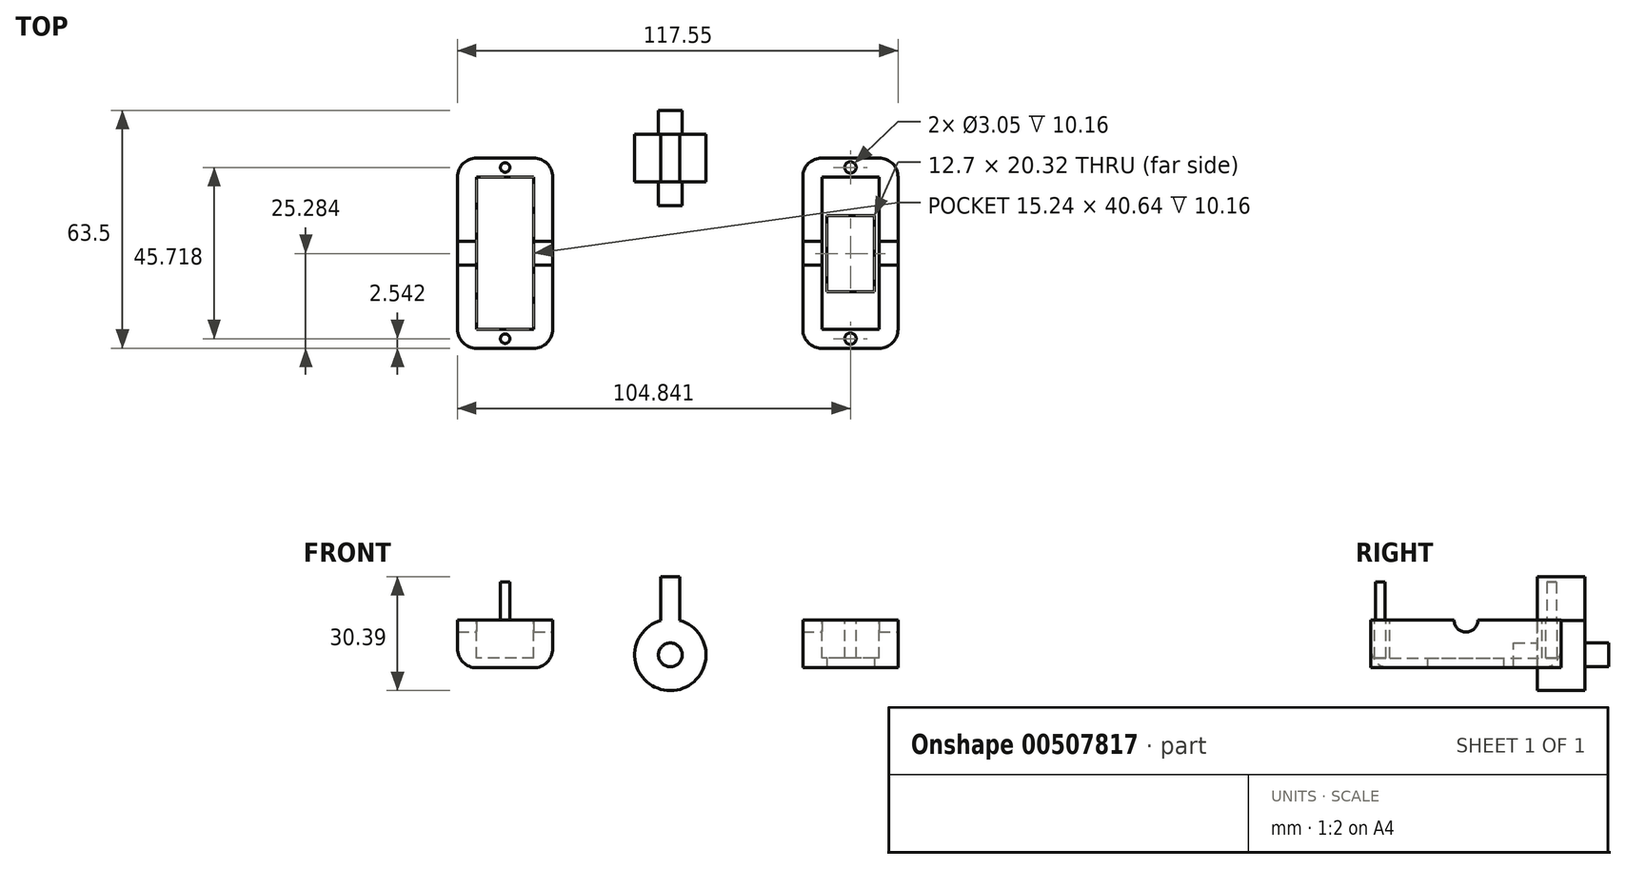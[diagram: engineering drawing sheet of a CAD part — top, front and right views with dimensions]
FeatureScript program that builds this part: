
annotation { "Feature Type Name" : "Feature", "Feature Type Description" : "" }
export const myFeature = defineFeature(function(context is Context, id is Id, definition is map)
    precondition{}
    {
        {
            var Q0;
            Q0=qCreatedBy(makeId("Front.planeOp"),FACE);
            var sketch = newSketch(context, id + "F0", { "sketchPlane" : qUnion([Q0])});
            skLineSegment(sketch, "E0", {"start": v(-56.79, 0) * mm, "end": v(-31.39, 0) * mm});
            skLineSegment(sketch, "E1", {"start": v(-31.39, 0) * mm, "end": v(-31.39, -12.7) * mm});
            skLineSegment(sketch, "E2", {"start": v(-31.39, -12.7) * mm, "end": v(-56.79, -12.7) * mm});
            skLineSegment(sketch, "E3", {"start": v(-56.79, -12.7) * mm, "end": v(-56.79, 0) * mm});
            skLineSegment(sketch, "E4", {"start": v(35.35, 0) * mm, "end": v(60.76, 0) * mm});
            skLineSegment(sketch, "E5", {"start": v(60.76, 0) * mm, "end": v(60.76, -12.7) * mm});
            skLineSegment(sketch, "E6", {"start": v(60.76, -12.7) * mm, "end": v(35.35, -12.7) * mm});
            skLineSegment(sketch, "E7", {"start": v(35.35, -12.7) * mm, "end": v(35.35, 0) * mm});
            skCircle(sketch, "E8", {"center": v(0, -9.27) * mm, "radius": 3.18 * mm});
            skCircle(sketch, "E9.0", {"center": v(0, -9.27) * mm, "radius": 9.52 * mm});
            skLineSegment(sketch, "E10", {"start": v(0, 0.26) * mm, "end": v(0, 9.15) * mm});
            skLineSegment(sketch, "E11", {"start": v(-2.54, 11.6) * mm, "end": v(-2.54, -0.09) * mm});
            skLineSegment(sketch, "E12", {"start": v(2.54, 9.15) * mm, "end": v(2.54, -0.09) * mm});
            skLineSegment(sketch, "E13", {"start": v(0, 9.15) * mm, "end": v(0, 11.6) * mm});
            skLineSegment(sketch, "E14", {"start": v(0, 11.6) * mm, "end": v(-2.54, 11.6) * mm});
            skLineSegment(sketch, "E15", {"start": v(2.54, 9.15) * mm, "end": v(2.54, 11.6) * mm});
            skLineSegment(sketch, "E16", {"start": v(2.54, 11.6) * mm, "end": v(0, 11.6) * mm});
            skSolve(sketch);
        }
        {
            var Q0;
            Q0=makeQuery(id+"F0.imprint","IMPRINT",FACE,{"disambiguationData":[TD([[makeQuery(id+"F0.imprint","IMPRINT",EDGE,{"derivedFrom":sQuery(id+"F0.wireOp",EDGE,"E4")}),-1.0]])]});
            var Q1;
            Q1=makeQuery(id+"F0.imprint","IMPRINT",FACE,{"disambiguationData":[TD([[makeQuery(id+"F0.imprint","IMPRINT",EDGE,{"derivedFrom":sQuery(id+"F0.wireOp",EDGE,"E0")}),-1.0]])]});
            extrude(context, id + "F1", {"entities" : qUnion([Q0, Q1]), "depth" : 50.8 * mm});
        }
        {
            var Q0;
            Q0=qCreatedBy(makeId("Top.planeOp"),FACE);
            var sketch = newSketch(context, id + "F2", { "sketchPlane" : qUnion([Q0])});
            skLineSegment(sketch, "E17.0", {"start": v(-36.47, -5.08) * mm, "end": v(-51.7, -5.08) * mm});
            skLineSegment(sketch, "E17.1", {"start": v(-36.47, -45.72) * mm, "end": v(-36.47, -5.08) * mm});
            skLineSegment(sketch, "E17.2", {"start": v(-51.7, -45.72) * mm, "end": v(-36.47, -45.72) * mm});
            skLineSegment(sketch, "E17.3", {"start": v(-51.7, -5.08) * mm, "end": v(-51.7, -45.72) * mm});
            skLineSegment(sketch, "E18.0", {"start": v(55.68, -5.08) * mm, "end": v(40.43, -5.08) * mm});
            skLineSegment(sketch, "E18.1", {"start": v(55.68, -45.72) * mm, "end": v(55.68, -5.08) * mm});
            skLineSegment(sketch, "E18.2", {"start": v(40.43, -45.72) * mm, "end": v(55.68, -45.72) * mm});
            skLineSegment(sketch, "E18.3", {"start": v(40.43, -5.08) * mm, "end": v(40.43, -45.72) * mm});
            skCircle(sketch, "E19", {"center": v(-44.09, -48.25) * mm, "radius": 1.27 * mm});
            skCircle(sketch, "E20", {"center": v(-44.09, -2.54) * mm, "radius": 1.27 * mm});
            skCircle(sketch, "E21", {"center": v(48.05, -2.54) * mm, "radius": 1.52 * mm});
            skCircle(sketch, "E22", {"center": v(48.05, -48.26) * mm, "radius": 1.52 * mm});
            skSolve(sketch);
        }
        {
            var Q0;
            Q0=makeQuery(id+"F2.imprint","IMPRINT",FACE,{"disambiguationData":[TD([[makeQuery(id+"F2.imprint","IMPRINT",EDGE,{"derivedFrom":sQuery(id+"F2.wireOp",EDGE,"E17.0")}),1.0]])]});
            extrude(context, id + "F3", {"entities" : qUnion([Q0]), "operationType" : NewBodyOperationType.REMOVE, "oppositeDirection" : true, "depth" : 10.16 * mm});
        }
        {
            var Q0;
            Q0=makeQuery(id+"F2.imprint","IMPRINT",FACE,{"disambiguationData":[TD([[makeQuery(id+"F2.imprint","IMPRINT",EDGE,{"derivedFrom":sQuery(id+"F2.wireOp",EDGE,"E18.0")}),1.0]])]});
            extrude(context, id + "F4", {"entities" : qUnion([Q0]), "operationType" : NewBodyOperationType.REMOVE, "oppositeDirection" : true, "depth" : 10.16 * mm});
        }
        {
            var Q0;
            Q0=makeQuery(id+"F1.opExtrude","SWEPT_FACE",FACE,{"disambiguationData":[OSD([sQuery(id+"F0.wireOp",EDGE,"E1")])]});
            var sketch = newSketch(context, id + "F5", { "sketchPlane" : qUnion([Q0])});
            skCircle(sketch, "E23", {"center": v(-25.4, 0) * mm, "radius": 3.18 * mm});
            skSolve(sketch);
        }
        {
            var Q0;
            {var subQ0=sQuery(id+"F5.wireOp",EDGE,"E23");var subQ1=makeQuery(id+"F1.opExtrude","SWEPT_EDGE",EDGE,{"disambiguationData":[OSD([sQuery(id+"F0.wireOp",EDGE,"E0"),sQuery(id+"F0.wireOp",EDGE,"E1")])]});var subQ2=makeQuery(id+"F5.imprint","INTERSECT",VERTEX,{"disambiguationData":[OD(0.0)],"derivedFrom":[subQ1,subQ0]});Q0=makeQuery(id+"F5.imprint","IMPRINT",FACE,{"disambiguationData":[TD([[makeQuery(id+"F5.imprint","IMPRINT",EDGE,{"disambiguationData":[TD([[subQ2,1.0]])],"derivedFrom":subQ0}),1.0]])]});}
            extrude(context, id + "F6", {"entities" : qUnion([Q0]), "operationType" : NewBodyOperationType.REMOVE, "oppositeDirection" : true, "depth" : 25.4 * mm});
        }
        {
            var Q0;
            Q0=makeQuery(id+"F1.opExtrude","SWEPT_FACE",FACE,{"disambiguationData":[OSD([sQuery(id+"F0.wireOp",EDGE,"E5")])]});
            var sketch = newSketch(context, id + "F7", { "sketchPlane" : qUnion([Q0])});
            skCircle(sketch, "E24", {"center": v(-25.4, 0) * mm, "radius": 3.18 * mm});
            skSolve(sketch);
        }
        {
            var Q0;
            {var subQ0=sQuery(id+"F7.wireOp",EDGE,"E24");var subQ1=makeQuery(id+"F1.opExtrude","SWEPT_EDGE",EDGE,{"disambiguationData":[OSD([sQuery(id+"F0.wireOp",EDGE,"E4"),sQuery(id+"F0.wireOp",EDGE,"E5")])]});var subQ2=makeQuery(id+"F7.imprint","INTERSECT",VERTEX,{"disambiguationData":[OD(0.0)],"derivedFrom":[subQ1,subQ0]});Q0=makeQuery(id+"F7.imprint","IMPRINT",FACE,{"disambiguationData":[TD([[makeQuery(id+"F7.imprint","IMPRINT",EDGE,{"disambiguationData":[TD([[subQ2,1.0]])],"derivedFrom":subQ0}),1.0]])]});}
            extrude(context, id + "F8", {"entities" : qUnion([Q0]), "operationType" : NewBodyOperationType.REMOVE, "oppositeDirection" : true, "depth" : 25.4 * mm});
        }
        {
            var Q0;
            Q0=makeQuery(id+"F1.opExtrude","SWEPT_FACE",FACE,{"disambiguationData":[OSD([sQuery(id+"F0.wireOp",EDGE,"E6")])]});
            var sketch = newSketch(context, id + "F9", { "sketchPlane" : qUnion([Q0])});
            skLineSegment(sketch, "E25", {"start": v(41.7, 25.52) * mm, "end": v(41.7, 15.36) * mm});
            skLineSegment(sketch, "E26", {"start": v(41.7, 25.52) * mm, "end": v(41.7, 35.68) * mm});
            skLineSegment(sketch, "E27", {"start": v(54.4, 15.36) * mm, "end": v(54.4, 25.52) * mm});
            skLineSegment(sketch, "E28", {"start": v(41.7, 35.68) * mm, "end": v(54.4, 35.68) * mm});
            skLineSegment(sketch, "E29", {"start": v(54.4, 35.68) * mm, "end": v(54.4, 25.52) * mm});
            skLineSegment(sketch, "E30", {"start": v(41.7, 15.36) * mm, "end": v(54.4, 15.36) * mm});
            skLineSegment(sketch, "E31", {"start": v(41.7, 25.52) * mm, "end": v(54.4, 25.52) * mm});
            skSolve(sketch);
        }
        {
            var Q0;
            Q0=makeQuery(id+"F1.opExtrude","CAP_EDGE",EDGE,{"disambiguationData":[OSD([sQuery(id+"F0.wireOp",EDGE,"E1")])],"isStart":false});
            var Q1;
            Q1=makeQuery(id+"F1.opExtrude","CAP_EDGE",EDGE,{"disambiguationData":[OSD([sQuery(id+"F0.wireOp",EDGE,"E3")])],"isStart":false});
            var Q2;
            Q2=makeQuery(id+"F1.opExtrude","CAP_EDGE",EDGE,{"disambiguationData":[OSD([sQuery(id+"F0.wireOp",EDGE,"E2")])],"isStart":false});
            var Q3;
            Q3=makeQuery(id+"F1.opExtrude","SWEPT_EDGE",EDGE,{"disambiguationData":[OSD([sQuery(id+"F0.wireOp",EDGE,"E2"),sQuery(id+"F0.wireOp",EDGE,"E3")])]});
            var Q4;
            Q4=makeQuery(id+"F1.opExtrude","CAP_EDGE",EDGE,{"disambiguationData":[OSD([sQuery(id+"F0.wireOp",EDGE,"E3")])],"isStart":true});
            var Q5;
            Q5=makeQuery(id+"F1.opExtrude","CAP_EDGE",EDGE,{"disambiguationData":[OSD([sQuery(id+"F0.wireOp",EDGE,"E2")])],"isStart":true});
            var Q6;
            Q6=makeQuery(id+"F1.opExtrude","CAP_EDGE",EDGE,{"disambiguationData":[OSD([sQuery(id+"F0.wireOp",EDGE,"E1")])],"isStart":true});
            var Q7;
            Q7=makeQuery(id+"F1.opExtrude","SWEPT_EDGE",EDGE,{"disambiguationData":[OSD([sQuery(id+"F0.wireOp",EDGE,"E1"),sQuery(id+"F0.wireOp",EDGE,"E2")])]});
            fillet(context, id + "F10", {"entities" : qUnion([Q0, Q1, Q2, Q3, Q4, Q5, Q6, Q7]), "radius" : 5.08 * mm, "tangentPropagation" : true, "allowEdgeOverflow" : false});
        }
        {
            var Q0;
            Q0=makeQuery(id+"F0.imprint","IMPRINT",FACE,{"disambiguationData":[TD([[makeQuery(id+"F0.imprint","IMPRINT",EDGE,{"derivedFrom":sQuery(id+"F0.wireOp",EDGE,"E8")}),-1.0]])]});
            var Q1;
            {var subQ0=sQuery(id+"F0.wireOp",EDGE,"E10");Q1=makeQuery(id+"F0.imprint","IMPRINT",FACE,{"disambiguationData":[TD([[makeQuery(id+"F0.imprint","IMPRINT",EDGE,{"derivedFrom":subQ0}),-1.0]])]});}
            var Q2;
            {var subQ0=sQuery(id+"F0.wireOp",EDGE,"E10");Q2=makeQuery(id+"F0.imprint","IMPRINT",FACE,{"disambiguationData":[TD([[makeQuery(id+"F0.imprint","IMPRINT",EDGE,{"derivedFrom":subQ0}),1.0]])]});}
            extrude(context, id + "F11", {"entities" : qUnion([Q0, Q1, Q2]), "depth" : 12.7 * mm, "offsetDistance" : 25.4 * mm, "symmetric" : true});
        }
        {
            var Q0;
            Q0=makeQuery(id+"F0.imprint","IMPRINT",FACE,{"disambiguationData":[TD([[makeQuery(id+"F0.imprint","IMPRINT",EDGE,{"derivedFrom":sQuery(id+"F0.wireOp",EDGE,"E8")}),1.0]])]});
            extrude(context, id + "F12", {"entities" : qUnion([Q0]), "operationType" : NewBodyOperationType.ADD, "depth" : 25.4 * mm, "offsetDistance" : 25.4 * mm, "symmetric" : true});
        }
        {
            var Q0;
            Q0=makeQuery(id+"F2.imprint","IMPRINT",FACE,{"disambiguationData":[TD([[makeQuery(id+"F2.imprint","IMPRINT",EDGE,{"derivedFrom":sQuery(id+"F2.wireOp",EDGE,"E20")}),1.0]])]});
            var Q1;
            Q1=makeQuery(id+"F2.imprint","IMPRINT",FACE,{"disambiguationData":[TD([[makeQuery(id+"F2.imprint","IMPRINT",EDGE,{"derivedFrom":sQuery(id+"F2.wireOp",EDGE,"E19")}),1.0]])]});
            extrude(context, id + "F13", {"entities" : qUnion([Q0, Q1]), "operationType" : NewBodyOperationType.ADD, "depth" : 10.16 * mm, "offsetDistance" : 25.4 * mm});
        }
        {
            var Q0;
            Q0=makeQuery(id+"F2.imprint","IMPRINT",FACE,{"disambiguationData":[TD([[makeQuery(id+"F2.imprint","IMPRINT",EDGE,{"derivedFrom":sQuery(id+"F2.wireOp",EDGE,"E22")}),1.0]])]});
            var Q1;
            Q1=makeQuery(id+"F2.imprint","IMPRINT",FACE,{"disambiguationData":[TD([[makeQuery(id+"F2.imprint","IMPRINT",EDGE,{"derivedFrom":sQuery(id+"F2.wireOp",EDGE,"E21")}),1.0]])]});
            extrude(context, id + "F14", {"entities" : qUnion([Q0, Q1]), "operationType" : NewBodyOperationType.REMOVE, "oppositeDirection" : true, "depth" : 10.16 * mm, "offsetDistance" : 25.4 * mm});
        }
        {
            var Q0;
            Q0=makeQuery(id+"F1.opExtrude","CAP_EDGE",EDGE,{"disambiguationData":[OSD([sQuery(id+"F0.wireOp",EDGE,"E7")])],"isStart":false});
            var Q1;
            Q1=makeQuery(id+"F1.opExtrude","CAP_EDGE",EDGE,{"disambiguationData":[OSD([sQuery(id+"F0.wireOp",EDGE,"E5")])],"isStart":true});
            var Q2;
            Q2=makeQuery(id+"F1.opExtrude","CAP_EDGE",EDGE,{"disambiguationData":[OSD([sQuery(id+"F0.wireOp",EDGE,"E7")])],"isStart":true});
            var Q3;
            Q3=makeQuery(id+"F1.opExtrude","CAP_EDGE",EDGE,{"disambiguationData":[OSD([sQuery(id+"F0.wireOp",EDGE,"E5")])],"isStart":false});
            fillet(context, id + "F15", {"entities" : qUnion([Q0, Q1, Q2, Q3]), "radius" : 5.08 * mm, "tangentPropagation" : true, "allowEdgeOverflow" : false});
        }
        {
            var Q0;
            Q0=makeQuery(id+"F9.imprint","IMPRINT",FACE,{"disambiguationData":[TD([[makeQuery(id+"F9.imprint","IMPRINT",EDGE,{"derivedFrom":sQuery(id+"F9.wireOp",EDGE,"E25")}),1.0]])]});
            var Q1;
            Q1=makeQuery(id+"F9.imprint","IMPRINT",FACE,{"disambiguationData":[TD([[makeQuery(id+"F9.imprint","IMPRINT",EDGE,{"derivedFrom":sQuery(id+"F9.wireOp",EDGE,"E26")}),-1.0]])]});
            extrude(context, id + "F16", {"entities" : qUnion([Q0, Q1]), "operationType" : NewBodyOperationType.REMOVE, "oppositeDirection" : true, "depth" : 25.4 * mm, "offsetDistance" : 25.4 * mm});
        }
    });
